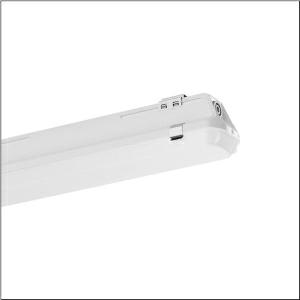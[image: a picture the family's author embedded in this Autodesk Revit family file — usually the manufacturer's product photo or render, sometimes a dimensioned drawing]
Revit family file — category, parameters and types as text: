
# Revit family: monsun_r__11_51fp10fp460h_036e
name_source: partatom
category: Lighting Fixtures
units: mm (PartAtom-declared; Revit-internal decimal feet)

## family parameters
Cut with Voids When Loaded = No
Host = Face
Light Source = No
Part Type = Normal
Room Calculation Point = No
Round Connector Dimension = Use Diameter
Shared = No

## types (1)
- --- (1 x LED, 6050 lm, 34.6 W, 4000K)
    Apparent Load = 35 VA
    CIE Flux Codes = 47 77 93 94 100
    Color Rendering = 80
    Color Temperature = 4000K
    Default Elevation = 1800 mm
    Description = Monsun® 11, damp-proof luminaire, chain hanger, primary optical cover: enclosure, of PMMA, light emission: direct distribution, primary light characteristic: symmetric, installation type: suspended mounting, surface-mounted, horizontal mounting, vertical mounting, LED, rated luminous flux: 6.050lm, luminous efficacy: 175lm/W, light colour: 840, colour temperature: 4000K, control gear: ECG DALI, with terminal, 5-pole, max. 2.5mm², mains connection: 220..240V, AC, 50/60Hz, start of lifetime: 35W, end of service life: 39W, luminaire housing, of glass-fibre reinforced polyester, uncoated, bright grey, incl. chain hanger, length: 1.590mm, width: 90mm, height: 88mm, clip for enclosure, of stainless steel (V2A), ceiling mounting element, of stainless steel (V2A), chain hanger, of stainless steel (V2A), protection rating (complete): IP66, insulation class (complete): insulation class I (protective earthing), certification: CE, ENEC, VDE, UKCA, protection symbol: D, impact resistance: IK04, permissible operating ambient temperature: -25..+40°C, standard: EN 50419, EN 60598-2-1, no direct snow, no direct sun, no direct rain, for indoor or canopied outdoor use, corresponds to IFS (International Featured Standards) requirements for safety and quality in the food industry, contact your sales advisor before using the luminaires in applications with unclear chemical exposure, large temperature fluctuations or condensation-forming humidity, LABS conformity tested according to VDMA 24364:2018-05, packaging unit: 1 piece
    Height = 89 mm
    Lamp = 1 x LED
    Lamp Light Flux = 6050 lm
    Lamp Power = 34.6 W
    Lamp count = 1
    Length = 1590 mm
    Luminous efficacy = 175 lm/W
    Manufacturer = Siteco
    ModVariant = No
    Model = 51FP10FP460H
    Mounting Place = Ceiling
    Mounting Type = Surface mounted
    Number of Poles = 1
    OnlyDefault = Yes
    Power Factor = 1
    Product Name = Monsun® 11
    Product group = damp-proof luminaire
    ProductGroupID = 301
    Protection Class = Protection class I
    Protection Degree = IP 66
    RLX_Detail_Level = 1
    RLX_Emergency_Light_Flux = 0 lm
    RLX_Emergency_Type = 0
    RLX_Emergency_Type_DB = No
    RlxData = <blob elided: 92305 chars, md5=b091915a>
    Socket = socket
    Standby Power = 0 W
    System Light Flux = 6050 lm
    System Power = 35 W
    Type Comments = factory setting: luminous flux: 100 % | dim-lin: 254 | 232 mA
    Type Image = l_1004748.jpg
    URL = http://relux.com
    VarID = @adj_157363
    Voltage = 0 V
    Weight = 0.00 kg
    Width = 90 mm

## geometry (parser evidence)
native form markers: Blend x4, Sweep x14
no freeform markers — native parametric forms only
